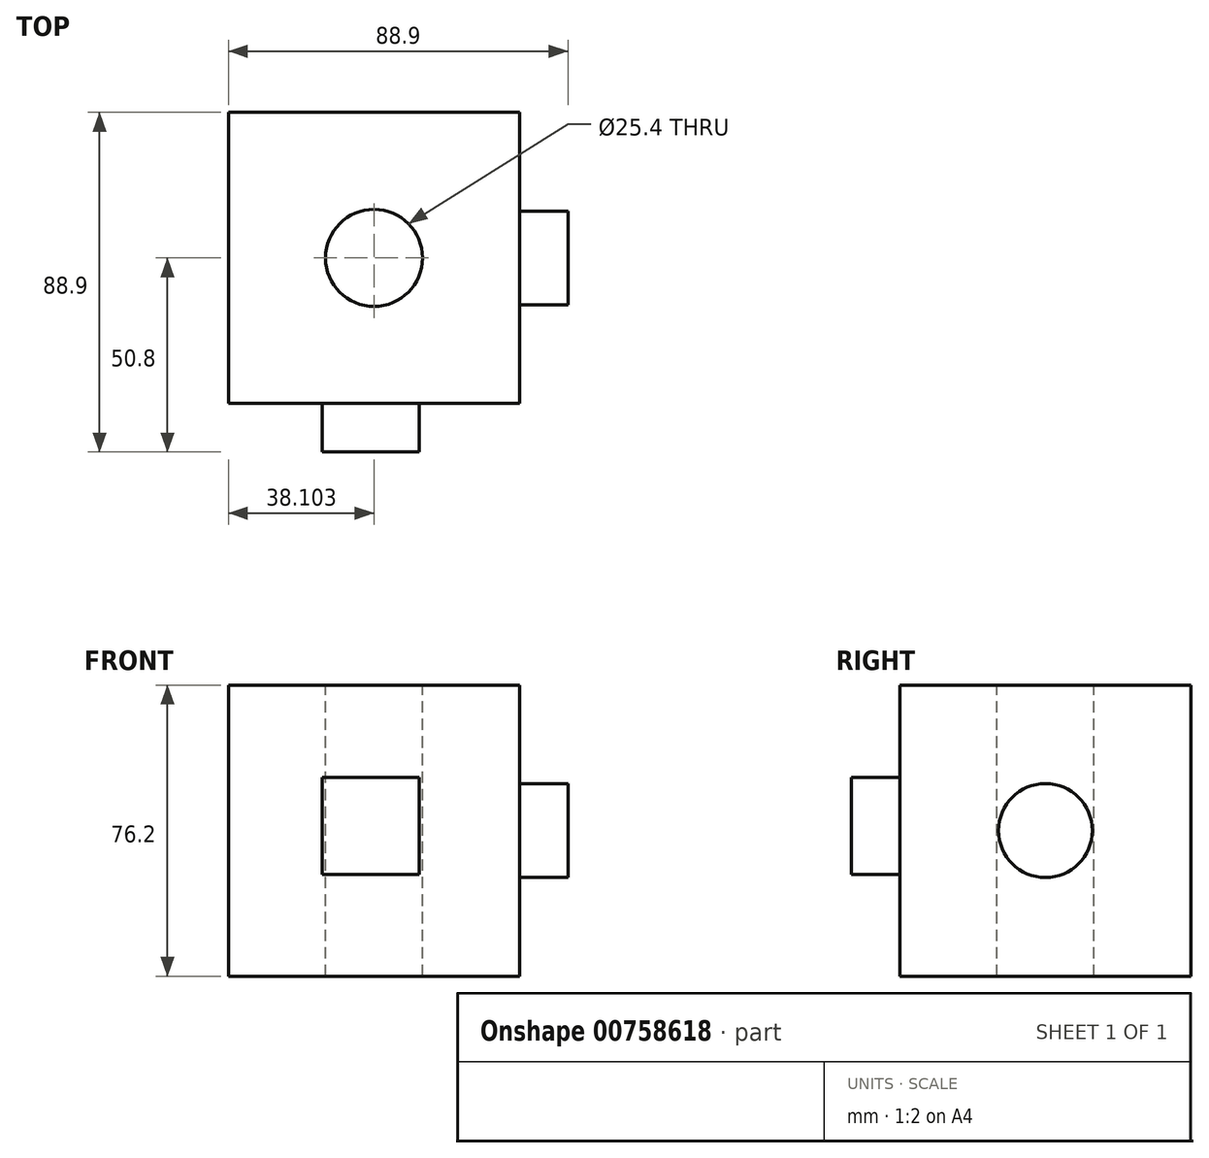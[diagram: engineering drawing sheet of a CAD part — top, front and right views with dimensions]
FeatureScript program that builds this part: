
annotation { "Feature Type Name" : "Feature", "Feature Type Description" : "" }
export const myFeature = defineFeature(function(context is Context, id is Id, definition is map)
    precondition{}
    {
        {
            var Q0;
            Q0=qCreatedBy(makeId("Front.planeOp"),FACE);
            var sketch = newSketch(context, id + "F0", { "sketchPlane" : qUnion([Q0])});
            skLineSegment(sketch, "E0.bottom", {"start": v(857.87, -592.03) * mm, "end": v(934.07, -592.03) * mm});
            skLineSegment(sketch, "E0.top", {"start": v(857.87, -668.23) * mm, "end": v(934.07, -668.23) * mm});
            skLineSegment(sketch, "E0.left", {"start": v(857.87, -592.03) * mm, "end": v(857.87, -668.23) * mm});
            skLineSegment(sketch, "E0.right", {"start": v(934.07, -592.03) * mm, "end": v(934.07, -668.23) * mm});
            skSolve(sketch);
        }
        {
            var Q0;
            Q0 = qSketchRegion(id + "F0", true);
            extrude(context, id + "F1", {"entities" : qUnion([Q0]), "depth" : 76.2 * mm, "offsetDistance" : 25.4 * mm});
        }
        {
            var Q0;
            Q0=makeQuery(id+"F1.opExtrude","CAP_FACE",FACE,{"disambiguationData":[OSD([sQuery(id+"F0.wireOp",EDGE,"E0.bottom"),sQuery(id+"F0.wireOp",EDGE,"E0.top"),sQuery(id+"F0.wireOp",EDGE,"E0.left"),sQuery(id+"F0.wireOp",EDGE,"E0.right")])],"isStart":false});
            var sketch = newSketch(context, id + "F2", { "sketchPlane" : qUnion([Q0])});
            skLineSegment(sketch, "E1.bottom", {"start": v(882.42, -616.22) * mm, "end": v(907.82, -616.22) * mm});
            skLineSegment(sketch, "E1.top", {"start": v(882.42, -641.62) * mm, "end": v(907.82, -641.62) * mm});
            skLineSegment(sketch, "E1.left", {"start": v(882.42, -616.22) * mm, "end": v(882.42, -641.62) * mm});
            skLineSegment(sketch, "E1.right", {"start": v(907.82, -616.22) * mm, "end": v(907.82, -641.62) * mm});
            skSolve(sketch);
        }
        {
            var Q0;
            Q0 = qSketchRegion(id + "F2", true);
            extrude(context, id + "F3", {"entities" : qUnion([Q0]), "operationType" : NewBodyOperationType.ADD, "depth" : 12.7 * mm, "offsetDistance" : 25.4 * mm});
        }
        {
            var Q0;
            Q0=makeQuery(id+"F1.opExtrude","SWEPT_FACE",FACE,{"disambiguationData":[OSD([sQuery(id+"F0.wireOp",EDGE,"E0.right")])]});
            var sketch = newSketch(context, id + "F4", { "sketchPlane" : qUnion([Q0])});
            skCircle(sketch, "E2", {"center": v(-38.1, -630.13) * mm, "radius": 12.3 * mm});
            skSolve(sketch);
        }
        {
            var Q0;
            Q0 = qSketchRegion(id + "F4", true);
            extrude(context, id + "F5", {"entities" : qUnion([Q0]), "operationType" : NewBodyOperationType.ADD, "depth" : 12.7 * mm, "offsetDistance" : 25.4 * mm});
        }
        {
            var Q0;
            Q0=makeQuery(id+"F1.opExtrude","SWEPT_FACE",FACE,{"disambiguationData":[OSD([sQuery(id+"F0.wireOp",EDGE,"E0.bottom")])]});
            var sketch = newSketch(context, id + "F6", { "sketchPlane" : qUnion([Q0])});
            skPoint(sketch, "E3", {"position": v(895.97, -38.1) * mm});
            skSolve(sketch);
        }
        {
            var Q0;
            Q0=sQuery(id+"F6.wireOp",VERTEX,"E3");
            var Q1;
            Q1=makeQuery(id+"F1.opExtrude","SWEPT_BODY",BODY,{"disambiguationData":[OSD([sQuery(id+"F0.wireOp",EDGE,"E0.bottom"),sQuery(id+"F0.wireOp",EDGE,"E0.top"),sQuery(id+"F0.wireOp",EDGE,"E0.left"),sQuery(id+"F0.wireOp",EDGE,"E0.right")])]});
            hole(context, id + "F7", {"style" : HoleStyle.SIMPLE, "endStyle" : HoleEndStyle.THROUGH, "holeDiameter" : 25.4 * mm, "majorDiameter" : 6.35 * mm, "isTappedThrough" : true, "tappedDepth" : 12.7 * mm, "tapClearance" : 3, "locations" : qUnion([Q0]), "scope" : qUnion([Q1])});
        }
    });
